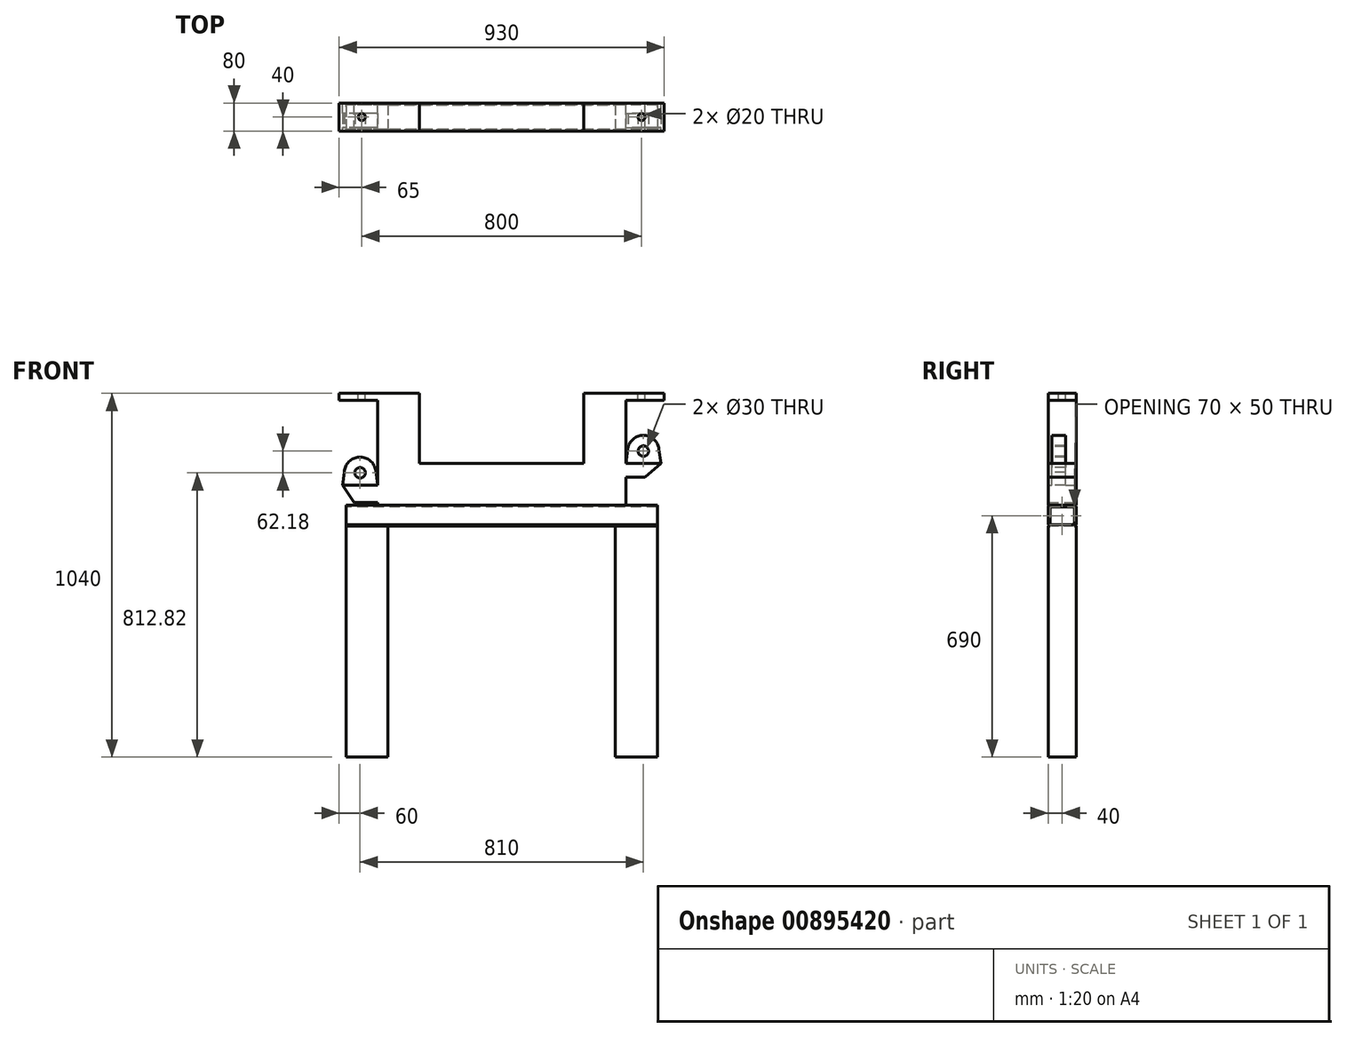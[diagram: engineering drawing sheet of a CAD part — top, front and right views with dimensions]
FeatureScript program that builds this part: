
annotation { "Feature Type Name" : "Feature", "Feature Type Description" : "" }
export const myFeature = defineFeature(function(context is Context, id is Id, definition is map)
    precondition{}
    {
        {
            var Q0;
            Q0=qCreatedBy(makeId("Front.planeOp"),FACE);
            var sketch = newSketch(context, id + "F0", { "sketchPlane" : qUnion([Q0])});
            skLineSegment(sketch, "E0.bottom", {"start": v(-355, 0) * mm, "end": v(-235, 0) * mm});
            skLineSegment(sketch, "E0.top", {"start": v(-355, -1040) * mm, "end": v(-235, -1040) * mm});
            skLineSegment(sketch, "E0.left", {"start": v(-355, -20) * mm, "end": v(-355, -262.18) * mm});
            skLineSegment(sketch, "E0.right", {"start": v(355, -20) * mm, "end": v(355, -200) * mm});
            skLineSegment(sketch, "E1.top", {"start": v(-235, -840) * mm, "end": v(235, -840) * mm});
            skLineSegment(sketch, "E1.left", {"start": v(-235, -1040) * mm, "end": v(-235, -840) * mm});
            skLineSegment(sketch, "E1.right", {"start": v(235, -1040) * mm, "end": v(235, -840) * mm});
            skLineSegment(sketch, "E2.bottom", {"start": v(-235, -720) * mm, "end": v(235, -720) * mm});
            skLineSegment(sketch, "E2.top", {"start": v(-235, -320) * mm, "end": v(235, -320) * mm});
            skLineSegment(sketch, "E2.left", {"start": v(-235, -720) * mm, "end": v(-235, -320) * mm});
            skLineSegment(sketch, "E2.right", {"start": v(235, -720) * mm, "end": v(235, -320) * mm});
            skLineSegment(sketch, "E3.bottom", {"start": v(-235, -200) * mm, "end": v(235, -200) * mm});
            skLineSegment(sketch, "E3.left", {"start": v(-235, -200) * mm, "end": v(-235, 0) * mm});
            skLineSegment(sketch, "E3.right", {"start": v(235, -200) * mm, "end": v(235, 0) * mm});
            skLineSegment(sketch, "E4.bottom", {"start": v(-355, 0) * mm, "end": v(-465, 0) * mm});
            skLineSegment(sketch, "E4.top", {"start": v(-355, -20) * mm, "end": v(-465, -20) * mm});
            skLineSegment(sketch, "E4.right", {"start": v(-465, 0) * mm, "end": v(-465, -20) * mm});
            skLineSegment(sketch, "E5.bottom", {"start": v(355, 0) * mm, "end": v(465, 0) * mm});
            skLineSegment(sketch, "E5.top", {"start": v(355, -20) * mm, "end": v(465, -20) * mm});
            skLineSegment(sketch, "E5.right", {"start": v(465, 0) * mm, "end": v(465, -20) * mm});
            skLineSegment(sketch, "E6.bottom", {"start": v(355, -1040) * mm, "end": v(415, -1040) * mm});
            skLineSegment(sketch, "E6.top", {"start": v(355, -1020) * mm, "end": v(415, -1020) * mm});
            skLineSegment(sketch, "E6.left", {"start": v(355, -1040) * mm, "end": v(355, -1020) * mm});
            skLineSegment(sketch, "E6.right", {"start": v(415, -1040) * mm, "end": v(415, -1020) * mm});
            skLineSegment(sketch, "E7.bottom", {"start": v(-355, -1040) * mm, "end": v(-415, -1040) * mm});
            skLineSegment(sketch, "E7.top", {"start": v(-355, -1020) * mm, "end": v(-415, -1020) * mm});
            skLineSegment(sketch, "E7.left", {"start": v(-355, -1040) * mm, "end": v(-355, -1020) * mm});
            skLineSegment(sketch, "E7.right", {"start": v(-415, -1040) * mm, "end": v(-415, -1020) * mm});
            skLineSegment(sketch, "E8.trimOffspring", {"start": v(235, 0) * mm, "end": v(355, 0) * mm});
            skLineSegment(sketch, "E9.trimOffspring", {"start": v(235, -1040) * mm, "end": v(355, -1040) * mm});
            skLineSegment(sketch, "E10.bottom", {"start": v(-355, -312.18) * mm, "end": v(-421.83, -312.18) * mm});
            skLineSegment(sketch, "E10.top", {"start": v(-355, -262.18) * mm, "end": v(-455, -262.18) * mm});
            skLineSegment(sketch, "E11", {"start": v(-455, -262.18) * mm, "end": v(-421.83, -312.18) * mm});
            skLineSegment(sketch, "E12.bottom", {"start": v(355, -200) * mm, "end": v(455, -200) * mm});
            skLineSegment(sketch, "E12.top", {"start": v(355, -240) * mm, "end": v(410.28, -240) * mm});
            skLineSegment(sketch, "E13", {"start": v(455, -200) * mm, "end": v(410.28, -240) * mm});
            skLineSegment(sketch, "E14.trimOffspring", {"start": v(-355, -312.18) * mm, "end": v(-355, -1040) * mm});
            skLineSegment(sketch, "E15.trimOffspring", {"start": v(355, -240) * mm, "end": v(355, -1040) * mm});
            skSolve(sketch);
        }
        {
            var Q0;
            Q0=qSketchRegion(id+"F0",true);
            extrude(context, id + "F1", {"entities" : qUnion([Q0]), "depth" : 80 * mm, "offsetDistance" : 25 * mm});
        }
        {
            var Q0;
            Q0=makeQuery(id+"F1.opExtrude","CAP_FACE",FACE,{"disambiguationData":[OSD([sQuery(id+"F0.wireOp",EDGE,"E0.bottom"),sQuery(id+"F0.wireOp",EDGE,"E0.top"),sQuery(id+"F0.wireOp",EDGE,"E0.left"),sQuery(id+"F0.wireOp",EDGE,"E0.right"),sQuery(id+"F0.wireOp",EDGE,"E1.top"),sQuery(id+"F0.wireOp",EDGE,"E1.left"),sQuery(id+"F0.wireOp",EDGE,"E1.right"),sQuery(id+"F0.wireOp",EDGE,"E2.bottom"),sQuery(id+"F0.wireOp",EDGE,"E2.top"),sQuery(id+"F0.wireOp",EDGE,"E2.left"),sQuery(id+"F0.wireOp",EDGE,"E2.right"),sQuery(id+"F0.wireOp",EDGE,"E3.bottom"),sQuery(id+"F0.wireOp",EDGE,"E3.left"),sQuery(id+"F0.wireOp",EDGE,"E3.right"),sQuery(id+"F0.wireOp",EDGE,"E4.bottom"),sQuery(id+"F0.wireOp",EDGE,"E4.top"),sQuery(id+"F0.wireOp",EDGE,"E4.right"),sQuery(id+"F0.wireOp",EDGE,"E5.bottom"),sQuery(id+"F0.wireOp",EDGE,"E5.top"),sQuery(id+"F0.wireOp",EDGE,"E5.right"),sQuery(id+"F0.wireOp",EDGE,"E6.bottom"),sQuery(id+"F0.wireOp",EDGE,"E6.top"),sQuery(id+"F0.wireOp",EDGE,"E6.right"),sQuery(id+"F0.wireOp",EDGE,"E7.bottom"),sQuery(id+"F0.wireOp",EDGE,"E7.top"),sQuery(id+"F0.wireOp",EDGE,"E7.right"),sQuery(id+"F0.wireOp",EDGE,"E8.trimOffspring"),sQuery(id+"F0.wireOp",EDGE,"E9.trimOffspring"),sQuery(id+"F0.wireOp",EDGE,"E10.bottom"),sQuery(id+"F0.wireOp",EDGE,"E10.top"),sQuery(id+"F0.wireOp",EDGE,"E11"),sQuery(id+"F0.wireOp",EDGE,"E12.bottom"),sQuery(id+"F0.wireOp",EDGE,"E12.top"),sQuery(id+"F0.wireOp",EDGE,"E13"),sQuery(id+"F0.wireOp",EDGE,"E14.trimOffspring"),sQuery(id+"F0.wireOp",EDGE,"E15.trimOffspring")])],"isStart":false});
            var sketch = newSketch(context, id + "F2", { "sketchPlane" : qUnion([Q0])});
            skLineSegment(sketch, "E16.bottom", {"start": v(-451.7, -1040) * mm, "end": v(537.4, -1040) * mm});
            skLineSegment(sketch, "E16.top", {"start": v(-451.7, -320) * mm, "end": v(537.4, -320) * mm});
            skLineSegment(sketch, "E16.left", {"start": v(-451.7, -1040) * mm, "end": v(-451.7, -320) * mm});
            skLineSegment(sketch, "E16.right", {"start": v(537.4, -1040) * mm, "end": v(537.4, -320) * mm});
            skSolve(sketch);
        }
        {
            var Q0;
            Q0 = qSketchRegion(id + "F2", true);
            extrude(context, id + "F3", {"entities" : qUnion([Q0]), "operationType" : NewBodyOperationType.REMOVE, "oppositeDirection" : true, "depth" : 80 * mm, "offsetDistance" : 25 * mm});
        }
        {
            var Q0;
            Q0=makeQuery(id+"F1.opExtrude","SWEPT_FACE",FACE,{"disambiguationData":[OSD([sQuery(id+"F0.wireOp",EDGE,"E0.bottom"),sQuery(id+"F0.wireOp",EDGE,"E4.bottom")])]});
            var sketch = newSketch(context, id + "F4", { "sketchPlane" : qUnion([Q0])});
            skCircle(sketch, "E17", {"center": v(-400, -40) * mm, "radius": 10 * mm});
            skCircle(sketch, "E18", {"center": v(400, -40) * mm, "radius": 10 * mm});
            skSolve(sketch);
        }
        {
            var Q0;
            Q0 = qSketchRegion(id + "F4", true);
            extrude(context, id + "F5", {"entities" : qUnion([Q0]), "operationType" : NewBodyOperationType.REMOVE, "oppositeDirection" : true, "depth" : 25 * mm, "offsetDistance" : 25 * mm});
        }
        {
            var Q0;
            Q0=makeQuery(id+"F1.opExtrude","CAP_FACE",FACE,{"disambiguationData":[OSD([sQuery(id+"F0.wireOp",EDGE,"E0.bottom"),sQuery(id+"F0.wireOp",EDGE,"E0.top"),sQuery(id+"F0.wireOp",EDGE,"E0.left"),sQuery(id+"F0.wireOp",EDGE,"E0.right"),sQuery(id+"F0.wireOp",EDGE,"E1.top"),sQuery(id+"F0.wireOp",EDGE,"E1.left"),sQuery(id+"F0.wireOp",EDGE,"E1.right"),sQuery(id+"F0.wireOp",EDGE,"E2.bottom"),sQuery(id+"F0.wireOp",EDGE,"E2.top"),sQuery(id+"F0.wireOp",EDGE,"E2.left"),sQuery(id+"F0.wireOp",EDGE,"E2.right"),sQuery(id+"F0.wireOp",EDGE,"E3.bottom"),sQuery(id+"F0.wireOp",EDGE,"E3.left"),sQuery(id+"F0.wireOp",EDGE,"E3.right"),sQuery(id+"F0.wireOp",EDGE,"E4.bottom"),sQuery(id+"F0.wireOp",EDGE,"E4.top"),sQuery(id+"F0.wireOp",EDGE,"E4.right"),sQuery(id+"F0.wireOp",EDGE,"E5.bottom"),sQuery(id+"F0.wireOp",EDGE,"E5.top"),sQuery(id+"F0.wireOp",EDGE,"E5.right"),sQuery(id+"F0.wireOp",EDGE,"E6.bottom"),sQuery(id+"F0.wireOp",EDGE,"E6.top"),sQuery(id+"F0.wireOp",EDGE,"E6.right"),sQuery(id+"F0.wireOp",EDGE,"E7.bottom"),sQuery(id+"F0.wireOp",EDGE,"E7.top"),sQuery(id+"F0.wireOp",EDGE,"E7.right"),sQuery(id+"F0.wireOp",EDGE,"E8.trimOffspring"),sQuery(id+"F0.wireOp",EDGE,"E9.trimOffspring"),sQuery(id+"F0.wireOp",EDGE,"E10.bottom"),sQuery(id+"F0.wireOp",EDGE,"E10.top"),sQuery(id+"F0.wireOp",EDGE,"E11"),sQuery(id+"F0.wireOp",EDGE,"E12.bottom"),sQuery(id+"F0.wireOp",EDGE,"E12.top"),sQuery(id+"F0.wireOp",EDGE,"E13"),sQuery(id+"F0.wireOp",EDGE,"E14.trimOffspring"),sQuery(id+"F0.wireOp",EDGE,"E15.trimOffspring")])],"isStart":false});
            var sketch = newSketch(context, id + "F6", { "sketchPlane" : qUnion([Q0])});
            skArc(sketch, "E19", {"start": v(-360.39, -221.3) * mm, "mid": v(-407.1, -182.23) * mm, "end": v(-449.97, -225.48) * mm});
            skLineSegment(sketch, "E20", {"start": v(-455, -262.18) * mm, "end": v(-449.97, -225.48) * mm});
            skLineSegment(sketch, "E21", {"start": v(-355, -262.18) * mm, "end": v(-360.39, -221.3) * mm});
            skCircle(sketch, "E22", {"center": v(-405, -227.18) * mm, "radius": 15 * mm});
            skArc(sketch, "E23", {"start": v(449.61, -159.12) * mm, "mid": v(408.68, -120.15) * mm, "end": v(361.94, -151.93) * mm});
            skPoint(sketch, "E23.centerSnap0", {"position": v(405, -200) * mm});
            skLineSegment(sketch, "E24", {"start": v(455, -200) * mm, "end": v(449.61, -159.12) * mm});
            skLineSegment(sketch, "E25", {"start": v(355, -200) * mm, "end": v(361.94, -151.93) * mm});
            skCircle(sketch, "E26", {"center": v(405, -165) * mm, "radius": 15 * mm});
            skSolve(sketch);
        }
        {
            var Q0;
            Q0=makeQuery(id+"F6.imprint","IMPRINT",FACE,{"disambiguationData":[TD([[makeQuery(id+"F6.imprint","IMPRINT",EDGE,{"derivedFrom":sQuery(id+"F6.wireOp",EDGE,"E19")}),1.0]])]});
            var Q1;
            Q1=makeQuery(id+"F6.imprint","IMPRINT",FACE,{"disambiguationData":[TD([[makeQuery(id+"F6.imprint","IMPRINT",EDGE,{"derivedFrom":sQuery(id+"F6.wireOp",EDGE,"E23")}),1.0]])]});
            extrude(context, id + "F7", {"entities" : qUnion([Q0, Q1]), "operationType" : NewBodyOperationType.ADD, "oppositeDirection" : true, "depth" : 50 * mm, "offsetDistance" : 25 * mm, "hasSecondDirection" : true, "secondDirectionOppositeDirection" : true, "secondDirectionDepth" : 10 * mm});
        }
        {
            var Q0;
            {var subQ0=sQuery(id+"F0.wireOp",EDGE,"E12.bottom");var subQ1=sQuery(id+"F0.wireOp",EDGE,"E10.top");Q0=makeQuery(id+"F7.boolean.opBoolean","MERGE",FACE,{"derivedFrom":[makeQuery(id+"F1.opExtrude","CAP_FACE",FACE,{"disambiguationData":[OSD([sQuery(id+"F0.wireOp",EDGE,"E0.bottom"),sQuery(id+"F0.wireOp",EDGE,"E0.top"),sQuery(id+"F0.wireOp",EDGE,"E0.left"),sQuery(id+"F0.wireOp",EDGE,"E0.right"),sQuery(id+"F0.wireOp",EDGE,"E1.top"),sQuery(id+"F0.wireOp",EDGE,"E1.left"),sQuery(id+"F0.wireOp",EDGE,"E1.right"),sQuery(id+"F0.wireOp",EDGE,"E2.bottom"),sQuery(id+"F0.wireOp",EDGE,"E2.top"),sQuery(id+"F0.wireOp",EDGE,"E2.left"),sQuery(id+"F0.wireOp",EDGE,"E2.right"),sQuery(id+"F0.wireOp",EDGE,"E3.bottom"),sQuery(id+"F0.wireOp",EDGE,"E3.left"),sQuery(id+"F0.wireOp",EDGE,"E3.right"),sQuery(id+"F0.wireOp",EDGE,"E4.bottom"),sQuery(id+"F0.wireOp",EDGE,"E4.top"),sQuery(id+"F0.wireOp",EDGE,"E4.right"),sQuery(id+"F0.wireOp",EDGE,"E5.bottom"),sQuery(id+"F0.wireOp",EDGE,"E5.top"),sQuery(id+"F0.wireOp",EDGE,"E5.right"),sQuery(id+"F0.wireOp",EDGE,"E6.bottom"),sQuery(id+"F0.wireOp",EDGE,"E6.top"),sQuery(id+"F0.wireOp",EDGE,"E6.right"),sQuery(id+"F0.wireOp",EDGE,"E7.bottom"),sQuery(id+"F0.wireOp",EDGE,"E7.top"),sQuery(id+"F0.wireOp",EDGE,"E7.right"),sQuery(id+"F0.wireOp",EDGE,"E8.trimOffspring"),sQuery(id+"F0.wireOp",EDGE,"E9.trimOffspring"),sQuery(id+"F0.wireOp",EDGE,"E10.bottom"),subQ1,sQuery(id+"F0.wireOp",EDGE,"E11"),subQ0,sQuery(id+"F0.wireOp",EDGE,"E12.top"),sQuery(id+"F0.wireOp",EDGE,"E13"),sQuery(id+"F0.wireOp",EDGE,"E14.trimOffspring"),sQuery(id+"F0.wireOp",EDGE,"E15.trimOffspring")])],"isStart":false}),makeQuery(id+"F7.opExtrude","CAP_FACE",FACE,{"disambiguationData":[OSD([subQ1,sQuery(id+"F6.wireOp",EDGE,"E19"),sQuery(id+"F6.wireOp",EDGE,"E20"),sQuery(id+"F6.wireOp",EDGE,"E21"),sQuery(id+"F6.wireOp",EDGE,"E22")])],"isStart":true}),makeQuery(id+"F7.opExtrude","CAP_FACE",FACE,{"disambiguationData":[OSD([subQ0,sQuery(id+"F6.wireOp",EDGE,"E23"),sQuery(id+"F6.wireOp",EDGE,"E24"),sQuery(id+"F6.wireOp",EDGE,"E25"),sQuery(id+"F6.wireOp",EDGE,"E26")])],"isStart":true})]});}
            var sketch = newSketch(context, id + "F8", { "sketchPlane" : qUnion([Q0])});
            skLineSegment(sketch, "E27.bottom", {"start": v(325, -380) * mm, "end": v(-325, -380) * mm});
            skLineSegment(sketch, "E27.top", {"start": v(-325, -1040) * mm, "end": v(325, -1040) * mm});
            skLineSegment(sketch, "E27.left", {"start": v(-325, -380) * mm, "end": v(-325, -1040) * mm});
            skLineSegment(sketch, "E27.right", {"start": v(325, -380) * mm, "end": v(325, -1040) * mm});
            skSolve(sketch);
        }
        {
            var Q0;
            Q0=makeQuery(id+"F8.imprint","IMPRINT",FACE,{"disambiguationData":[TD([[makeQuery(id+"F8.imprint","IMPRINT",EDGE,{"derivedFrom":makeQuery(id+"F1.opExtrude","CAP_EDGE",EDGE,{"disambiguationData":[OSD([sQuery(id+"F0.wireOp",EDGE,"E0.left")])],"isStart":false})}),1.0]])]});
            var sketch = newSketch(context, id + "F9", { "sketchPlane" : qUnion([Q0])});
            skLineSegment(sketch, "E28.bottom", {"start": v(-445, -320) * mm, "end": v(445, -320) * mm});
            skLineSegment(sketch, "E28.top", {"start": v(-325, -380) * mm, "end": v(325, -380) * mm});
            skLineSegment(sketch, "E28.left", {"start": v(-445, -320) * mm, "end": v(-445, -380) * mm});
            skLineSegment(sketch, "E28.right", {"start": v(445, -320) * mm, "end": v(445, -380) * mm});
            skLineSegment(sketch, "E29.top", {"start": v(-445, -1040) * mm, "end": v(-325, -1040) * mm});
            skLineSegment(sketch, "E29.left", {"start": v(-445, -380) * mm, "end": v(-445, -1040) * mm});
            skLineSegment(sketch, "E29.right", {"start": v(-325, -380) * mm, "end": v(-325, -1040) * mm});
            skLineSegment(sketch, "E30.top", {"start": v(445, -1040) * mm, "end": v(325, -1040) * mm});
            skLineSegment(sketch, "E30.left", {"start": v(445, -380) * mm, "end": v(445, -1040) * mm});
            skLineSegment(sketch, "E30.right", {"start": v(325, -380) * mm, "end": v(325, -1040) * mm});
            skSolve(sketch);
        }
        {
            var Q0;
            Q0=makeQuery(id+"F9.imprint","IMPRINT",FACE,{"disambiguationData":[TD([[makeQuery(id+"F9.imprint","IMPRINT",EDGE,{"derivedFrom":sQuery(id+"F9.wireOp",EDGE,"E28.top")}),1.0]])]});
            extrude(context, id + "F10", {"entities" : qUnion([Q0]), "operationType" : NewBodyOperationType.ADD, "oppositeDirection" : true, "depth" : 80 * mm, "offsetDistance" : 25 * mm});
        }
        {
            var Q0;
            Q0=makeQuery(id+"F10.opExtrude","SWEPT_FACE",FACE,{"disambiguationData":[OSD([sQuery(id+"F9.wireOp",EDGE,"E28.left"),sQuery(id+"F9.wireOp",EDGE,"E29.left")])]});
            var sketch = newSketch(context, id + "F11", { "sketchPlane" : qUnion([Q0])});
            skLineSegment(sketch, "E31.bottom", {"start": v(10, -325) * mm, "end": v(70, -325) * mm});
            skLineSegment(sketch, "E31.top", {"start": v(10, -375) * mm, "end": v(70, -375) * mm});
            skLineSegment(sketch, "E31.left", {"start": v(5, -330) * mm, "end": v(5, -370) * mm});
            skLineSegment(sketch, "E31.right", {"start": v(75, -330) * mm, "end": v(75, -370) * mm});
            skPoint(sketch, "E32.visualSharp", {"position": v(5, -325) * mm});
            skArc(sketch, "E32.filletArc", {"start": v(10, -325) * mm, "mid": v(6.46, -326.46) * mm, "end": v(5, -330) * mm});
            skPoint(sketch, "E33.visualSharp", {"position": v(5, -375) * mm});
            skArc(sketch, "E33.filletArc", {"start": v(5, -370) * mm, "mid": v(6.46, -373.54) * mm, "end": v(10, -375) * mm});
            skPoint(sketch, "E34.visualSharp", {"position": v(75, -375) * mm});
            skArc(sketch, "E34.filletArc", {"start": v(70, -375) * mm, "mid": v(73.54, -373.54) * mm, "end": v(75, -370) * mm});
            skPoint(sketch, "E35.visualSharp", {"position": v(75, -325) * mm});
            skArc(sketch, "E35.filletArc", {"start": v(75, -330) * mm, "mid": v(73.54, -326.46) * mm, "end": v(70, -325) * mm});
            skSolve(sketch);
        }
        {
            var Q0;
            Q0=makeQuery(id+"F11.imprint","IMPRINT",FACE,{"disambiguationData":[TD([[makeQuery(id+"F11.imprint","IMPRINT",EDGE,{"derivedFrom":sQuery(id+"F11.wireOp",EDGE,"E31.bottom")}),-1.0]])]});
            extrude(context, id + "F12", {"entities" : qUnion([Q0]), "operationType" : NewBodyOperationType.REMOVE, "oppositeDirection" : true, "depth" : 890 * mm, "offsetDistance" : 25 * mm});
        }
        {
            var Q0;
            {var subQ2=sQuery(id+"F9.wireOp",EDGE,"E28.bottom");var subQ3=sQuery(id+"F0.wireOp",EDGE,"E14.trimOffspring");Q0=makeQuery(id+"F10.boolean.opBoolean","SPLIT",EDGE,{"disambiguationData":[TD([makeQuery(id+"F1.opExtrude","SWEPT_FACE",FACE,{"disambiguationData":[OSD([subQ3])]})])],"derivedFrom":makeQuery(id+"F10.opExtrude","CAP_EDGE",EDGE,{"disambiguationData":[OSD([subQ2])],"isStart":true})});}
            var Q1;
            {var subQ0=sQuery(id+"F9.wireOp",EDGE,"E28.bottom");var subQ1=sQuery(id+"F0.wireOp",EDGE,"E14.trimOffspring");Q1=makeQuery(id+"F10.boolean.opBoolean","SPLIT",EDGE,{"disambiguationData":[TD([makeQuery(id+"F1.opExtrude","SWEPT_FACE",FACE,{"disambiguationData":[OSD([subQ1])]})])],"derivedFrom":makeQuery(id+"F10.opExtrude","CAP_EDGE",EDGE,{"disambiguationData":[OSD([subQ0])],"isStart":false})});}
            var Q2;
            Q2=makeQuery(id+"F10.opExtrude","CAP_EDGE",EDGE,{"disambiguationData":[OSD([sQuery(id+"F9.wireOp",EDGE,"E28.top")])],"isStart":true});
            var Q3;
            Q3=makeQuery(id+"F10.opExtrude","CAP_EDGE",EDGE,{"disambiguationData":[OSD([sQuery(id+"F9.wireOp",EDGE,"E28.top")])],"isStart":false});
            var Q4;
            {var subQ2=sQuery(id+"F9.wireOp",EDGE,"E28.bottom");var subQ3=sQuery(id+"F0.wireOp",EDGE,"E15.trimOffspring");Q4=makeQuery(id+"F10.boolean.opBoolean","SPLIT",EDGE,{"disambiguationData":[TD([makeQuery(id+"F1.opExtrude","SWEPT_FACE",FACE,{"disambiguationData":[OSD([subQ3])]})])],"derivedFrom":makeQuery(id+"F10.opExtrude","CAP_EDGE",EDGE,{"disambiguationData":[OSD([subQ2])],"isStart":true})});}
            var Q5;
            {var subQ0=sQuery(id+"F9.wireOp",EDGE,"E28.bottom");var subQ1=sQuery(id+"F0.wireOp",EDGE,"E15.trimOffspring");Q5=makeQuery(id+"F10.boolean.opBoolean","SPLIT",EDGE,{"disambiguationData":[TD([makeQuery(id+"F1.opExtrude","SWEPT_FACE",FACE,{"disambiguationData":[OSD([subQ1])]})])],"derivedFrom":makeQuery(id+"F10.opExtrude","CAP_EDGE",EDGE,{"disambiguationData":[OSD([subQ0])],"isStart":false})});}
            fillet(context, id + "F13", {"entities" : qUnion([Q0, Q1, Q2, Q3, Q4, Q5]), "radius" : 5 * mm, "tangentPropagation" : true, "allowEdgeOverflow" : false});
        }
        {
            var Q0;
            Q0=makeQuery(id+"F10.opExtrude","SWEPT_FACE",FACE,{"disambiguationData":[OSD([sQuery(id+"F9.wireOp",EDGE,"E28.left"),sQuery(id+"F9.wireOp",EDGE,"E29.left")])]});
            var sketch = newSketch(context, id + "F14", { "sketchPlane" : qUnion([Q0])});
            skLineSegment(sketch, "E36", {"start": v(80, -380) * mm, "end": v(75, -380) * mm});
            skLineSegment(sketch, "E37", {"start": v(75, -380) * mm, "end": v(80, -375) * mm});
            skLineSegment(sketch, "E38", {"start": v(80, -375) * mm, "end": v(80, -380) * mm});
            skLineSegment(sketch, "E39", {"start": v(0, -380) * mm, "end": v(5, -380) * mm});
            skLineSegment(sketch, "E40", {"start": v(5, -380) * mm, "end": v(0, -375) * mm});
            skLineSegment(sketch, "E41", {"start": v(0, -375) * mm, "end": v(0, -380) * mm});
            skSolve(sketch);
        }
        {
            var Q0;
            Q0 = qSketchRegion(id + "F14", true);
            extrude(context, id + "F15", {"entities" : qUnion([Q0]), "operationType" : NewBodyOperationType.REMOVE, "oppositeDirection" : true, "depth" : 1000 * mm, "offsetDistance" : 25 * mm});
        }
        {
            var Q0;
            Q0=makeQuery(id+"F10.opExtrude","SWEPT_FACE",FACE,{"disambiguationData":[OSD([sQuery(id+"F9.wireOp",EDGE,"E28.left"),sQuery(id+"F9.wireOp",EDGE,"E29.left")])]});
            var sketch = newSketch(context, id + "F16", { "sketchPlane" : qUnion([Q0])});
            skArc(sketch, "E42.0", {"start": v(80, -325) * mm, "mid": v(78.54, -321.46) * mm, "end": v(75, -320) * mm});
            skLineSegment(sketch, "E43.0", {"start": v(80, -312.18) * mm, "end": v(80, -325) * mm});
            skLineSegment(sketch, "E44", {"start": v(75, -320) * mm, "end": v(80, -320) * mm});
            skArc(sketch, "E45.0", {"start": v(5, -320) * mm, "mid": v(1.46, -321.46) * mm, "end": v(0, -325) * mm});
            skLineSegment(sketch, "E46.0", {"start": v(0, -312.18) * mm, "end": v(0, -325) * mm});
            skLineSegment(sketch, "E47", {"start": v(5, -320) * mm, "end": v(0, -320) * mm});
            skSolve(sketch);
        }
        {
            var Q0;
            Q0 = qSketchRegion(id + "F16", true);
            extrude(context, id + "F17", {"entities" : qUnion([Q0]), "operationType" : NewBodyOperationType.REMOVE, "oppositeDirection" : true, "depth" : 890 * mm, "offsetDistance" : 25 * mm});
        }
    });
